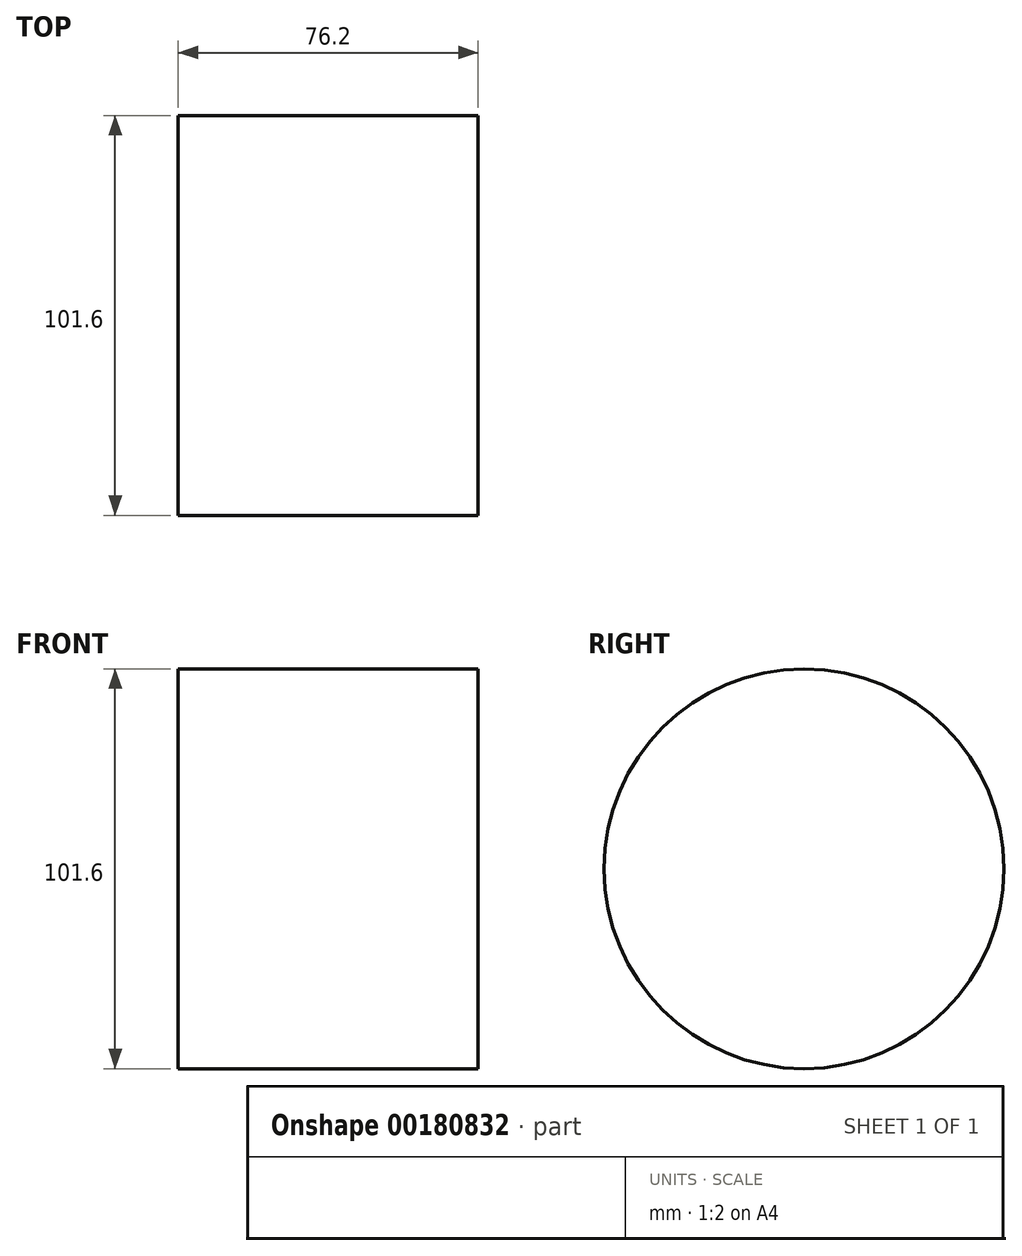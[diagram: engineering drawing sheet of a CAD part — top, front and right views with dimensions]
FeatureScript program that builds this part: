
annotation { "Feature Type Name" : "Feature", "Feature Type Description" : "" }
export const myFeature = defineFeature(function(context is Context, id is Id, definition is map)
    precondition{}
    {
        {
            var Q0;
            Q0=qCreatedBy(makeId("Right.planeOp"),FACE);
            var sketch = newSketch(context, id + "F0", { "sketchPlane" : qUnion([Q0])});
            skCircle(sketch, "E0", {"center": v(0, 0) * mm, "radius": 50.8 * mm});
            skSolve(sketch);
        }
        {
            var Q0;
            Q0=makeQuery(id+"F0.imprint","IMPRINT",FACE,{"disambiguationData":[TD([[makeQuery(id+"F0.imprint","IMPRINT",EDGE,{"derivedFrom":sQuery(id+"F0.wireOp",EDGE,"E0")}),1.0]])]});
            extrude(context, id + "F1", {"entities" : qUnion([Q0]), "depth" : 76.2 * mm});
        }
    });
